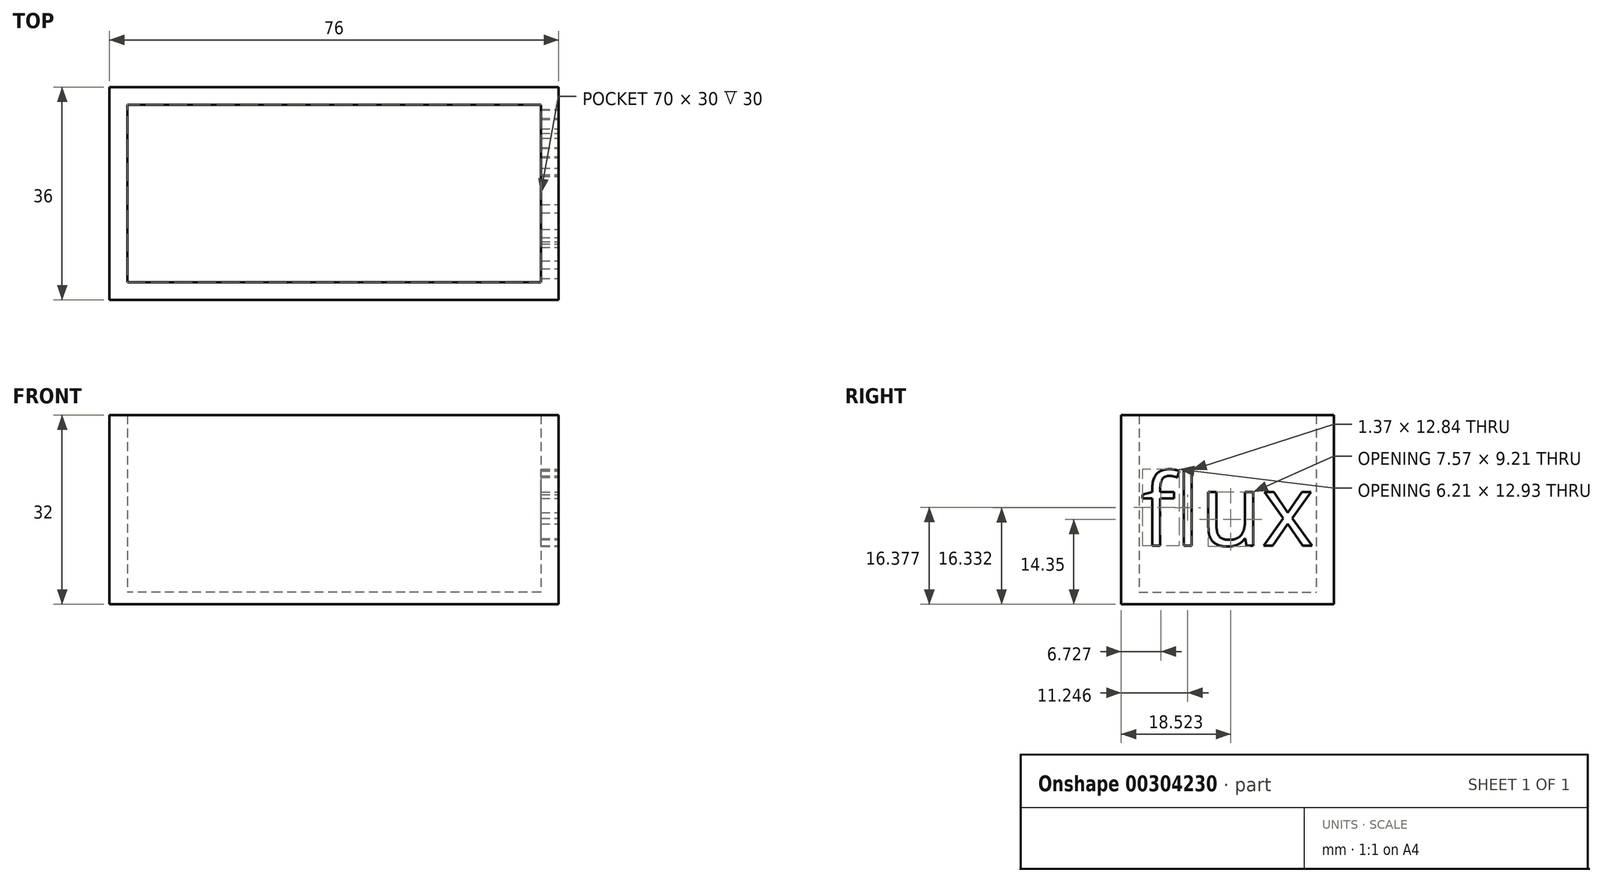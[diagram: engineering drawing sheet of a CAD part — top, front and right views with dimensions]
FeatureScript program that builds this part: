
annotation { "Feature Type Name" : "Feature", "Feature Type Description" : "" }
export const myFeature = defineFeature(function(context is Context, id is Id, definition is map)
    precondition{}
    {
        {
            var Q0;
            Q0=qCreatedBy(makeId("Top.planeOp"),FACE);
            var sketch = newSketch(context, id + "F0", { "sketchPlane" : qUnion([Q0])});
            skLineSegment(sketch, "E0.bottom", {"start": v(35, -15) * mm, "end": v(-35, -15) * mm});
            skLineSegment(sketch, "E0.top", {"start": v(35, 15) * mm, "end": v(-35, 15) * mm});
            skLineSegment(sketch, "E0.left", {"start": v(35, -15) * mm, "end": v(35, 15) * mm});
            skLineSegment(sketch, "E0.right", {"start": v(-35, -15) * mm, "end": v(-35, 15) * mm});
            skPoint(sketch, "E0.middle", {"position": v(0, 0) * mm});
            skLineSegment(sketch, "E1.0", {"start": v(38, 18) * mm, "end": v(-38, 18) * mm});
            skLineSegment(sketch, "E1.1", {"start": v(38, -18) * mm, "end": v(38, 18) * mm});
            skLineSegment(sketch, "E1.2", {"start": v(38, -18) * mm, "end": v(-38, -18) * mm});
            skLineSegment(sketch, "E1.3", {"start": v(-38, -18) * mm, "end": v(-38, 18) * mm});
            skSolve(sketch);
        }
        {
            var Q0;
            Q0 = qSketchRegion(id + "F0", true);
            extrude(context, id + "F1", {"entities" : qUnion([Q0]), "endBound" : BoundingType.SYMMETRIC, "depth" : 30 * mm});
        }
        {
            var Q0;
            Q0=makeQuery(id+"F1.opExtrude","CAP_FACE",FACE,{"disambiguationData":[OSD([sQuery(id+"F0.wireOp",EDGE,"E0.bottom"),sQuery(id+"F0.wireOp",EDGE,"E0.top"),sQuery(id+"F0.wireOp",EDGE,"E0.left"),sQuery(id+"F0.wireOp",EDGE,"E0.right"),sQuery(id+"F0.wireOp",EDGE,"E1.0"),sQuery(id+"F0.wireOp",EDGE,"E1.1"),sQuery(id+"F0.wireOp",EDGE,"E1.2"),sQuery(id+"F0.wireOp",EDGE,"E1.3")])],"isStart":true});
            var sketch = newSketch(context, id + "F2", { "sketchPlane" : qUnion([Q0])});
            skLineSegment(sketch, "E2.0.0", {"start": v(-38, 18) * mm, "end": v(-38, -18) * mm});
            skLineSegment(sketch, "E2.0.1", {"start": v(-38, -18) * mm, "end": v(38, -18) * mm});
            skLineSegment(sketch, "E2.0.2", {"start": v(38, -18) * mm, "end": v(38, 18) * mm});
            skLineSegment(sketch, "E2.0.3", {"start": v(38, 18) * mm, "end": v(-38, 18) * mm});
            skSolve(sketch);
        }
        {
            var Q0;
            Q0 = qSketchRegion(id + "F2", true);
            extrude(context, id + "F3", {"entities" : qUnion([Q0]), "operationType" : NewBodyOperationType.ADD, "depth" : 2 * mm});
        }
        {
            var Q0;
            Q0=makeQuery(id+"F3.boolean.opBoolean","MERGE",FACE,{"derivedFrom":[makeQuery(id+"F1.opExtrude","SWEPT_FACE",FACE,{"disambiguationData":[OSD([sQuery(id+"F0.wireOp",EDGE,"E1.1")])]}),makeQuery(id+"F3.opExtrude","SWEPT_FACE",FACE,{"disambiguationData":[OSD([sQuery(id+"F2.wireOp",EDGE,"E2.0.2")])]})]});
            var sketch = newSketch(context, id + "F4", { "sketchPlane" : qUnion([Q0])});
            skText(sketch, "E3", { "text": "flux", "fontName": "OpenSans-Regular.ttf"});
            const initialGuessF4  = {"E3": [-0.01462, -0.00709, 1, 0, 0.01217]};
            skSetInitialGuess(sketch, initialGuessF4);
            skSolve(sketch);
        }
        {
            var Q0;
            Q0 = qSketchRegion(id + "F4", true);
            extrude(context, id + "F5", {"entities" : qUnion([Q0]), "operationType" : NewBodyOperationType.REMOVE, "oppositeDirection" : true, "depth" : 5 * mm});
        }
    });
